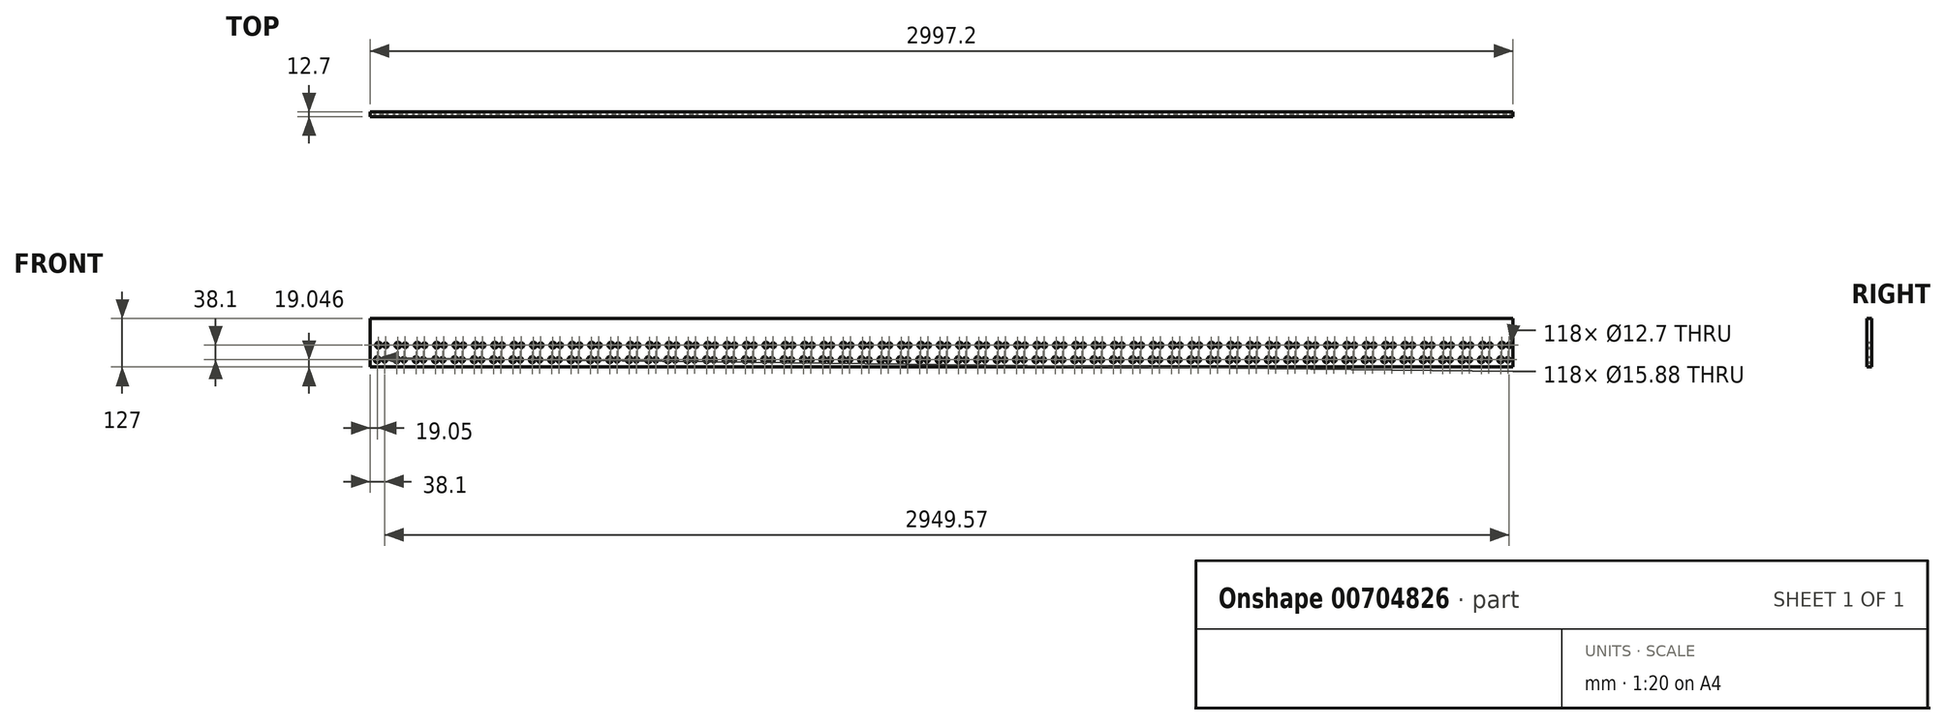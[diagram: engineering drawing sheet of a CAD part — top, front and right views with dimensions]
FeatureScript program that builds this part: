
annotation { "Feature Type Name" : "Feature", "Feature Type Description" : "" }
export const myFeature = defineFeature(function(context is Context, id is Id, definition is map)
    precondition{}
    {
        {
            var Q0;
            Q0=qCreatedBy(makeId("Front.planeOp"),FACE);
            var sketch = newSketch(context, id + "F0", { "sketchPlane" : qUnion([Q0])});
            skLineSegment(sketch, "E0.bottom", {"start": v(0, 309.84) * mm, "end": v(2997.2, 309.84) * mm});
            skLineSegment(sketch, "E0.top", {"start": v(0, 182.84) * mm, "end": v(2997.2, 182.84) * mm});
            skLineSegment(sketch, "E0.left", {"start": v(0, 309.84) * mm, "end": v(0, 182.84) * mm});
            skLineSegment(sketch, "E0.right", {"start": v(2997.2, 309.84) * mm, "end": v(2997.2, 182.84) * mm});
            skLineSegment(sketch, "E1.0", {"start": v(19.05, 201.89) * mm, "end": v(1200.15, 201.89) * mm});
            skCircle(sketch, "E2", {"center": v(19.05, 201.89) * mm, "radius": 7.94 * mm});
            skCircle(sketch, "E3", {"center": v(38.1, 201.89) * mm, "radius": 6.35 * mm});
            skLineSegment(sketch, "E4.direction1", {"start": v(19.05, 201.89) * mm, "end": v(69.85, 201.89) * mm, "construction": true});
            skLineSegment(sketch, "E5.0", {"start": v(19.05, 220.94) * mm, "end": v(1200.15, 220.94) * mm});
            skLineSegment(sketch, "E6.MirrorCS", {"start": v(19.05, 239.99) * mm, "end": v(1200.15, 239.99) * mm});
            skCircle(sketch, "E7.MirrorC", {"center": v(41.28, 239.99) * mm, "radius": 6.35 * mm});
            skCircle(sketch, "E8.MirrorC", {"center": v(22.23, 239.99) * mm, "radius": 7.94 * mm});
            skCircle(sketch, "E9.1.0.0", {"center": v(92.08, 239.99) * mm, "radius": 6.35 * mm});
            skCircle(sketch, "E9.1.0.1", {"center": v(73.03, 239.99) * mm, "radius": 7.94 * mm});
            skCircle(sketch, "E9.2.0.0", {"center": v(142.88, 239.99) * mm, "radius": 6.35 * mm});
            skCircle(sketch, "E9.2.0.1", {"center": v(123.83, 239.99) * mm, "radius": 7.94 * mm});
            skCircle(sketch, "E9.3.0.0", {"center": v(193.68, 239.99) * mm, "radius": 6.35 * mm});
            skCircle(sketch, "E9.3.0.1", {"center": v(174.63, 239.99) * mm, "radius": 7.94 * mm});
            skCircle(sketch, "E9.4.0.0", {"center": v(244.48, 239.99) * mm, "radius": 6.35 * mm});
            skCircle(sketch, "E9.4.0.1", {"center": v(225.43, 239.99) * mm, "radius": 7.94 * mm});
            skCircle(sketch, "E9.5.0.0", {"center": v(295.28, 239.99) * mm, "radius": 6.35 * mm});
            skCircle(sketch, "E9.5.0.1", {"center": v(276.23, 239.99) * mm, "radius": 7.94 * mm});
            skCircle(sketch, "E9.6.0.0", {"center": v(346.08, 239.99) * mm, "radius": 6.35 * mm});
            skCircle(sketch, "E9.6.0.1", {"center": v(327.03, 239.99) * mm, "radius": 7.94 * mm});
            skCircle(sketch, "E9.7.0.0", {"center": v(396.88, 239.99) * mm, "radius": 6.35 * mm});
            skCircle(sketch, "E9.7.0.1", {"center": v(377.83, 239.99) * mm, "radius": 7.94 * mm});
            skCircle(sketch, "E9.8.0.0", {"center": v(447.68, 239.99) * mm, "radius": 6.35 * mm});
            skCircle(sketch, "E9.8.0.1", {"center": v(428.63, 239.99) * mm, "radius": 7.94 * mm});
            skCircle(sketch, "E9.9.0.0", {"center": v(498.48, 239.99) * mm, "radius": 6.35 * mm});
            skCircle(sketch, "E9.9.0.1", {"center": v(479.43, 239.99) * mm, "radius": 7.94 * mm});
            skCircle(sketch, "E9.10.0.0", {"center": v(549.28, 239.99) * mm, "radius": 6.35 * mm});
            skCircle(sketch, "E9.10.0.1", {"center": v(530.23, 239.99) * mm, "radius": 7.94 * mm});
            skCircle(sketch, "E9.11.0.0", {"center": v(600.08, 239.99) * mm, "radius": 6.35 * mm});
            skCircle(sketch, "E9.11.0.1", {"center": v(581.03, 239.99) * mm, "radius": 7.94 * mm});
            skCircle(sketch, "E9.12.0.0", {"center": v(650.88, 239.99) * mm, "radius": 6.35 * mm});
            skCircle(sketch, "E9.12.0.1", {"center": v(631.83, 239.99) * mm, "radius": 7.94 * mm});
            skCircle(sketch, "E9.13.0.0", {"center": v(701.68, 239.99) * mm, "radius": 6.35 * mm});
            skCircle(sketch, "E9.13.0.1", {"center": v(682.63, 239.99) * mm, "radius": 7.94 * mm});
            skCircle(sketch, "E9.14.0.0", {"center": v(752.48, 239.99) * mm, "radius": 6.35 * mm});
            skCircle(sketch, "E9.14.0.1", {"center": v(733.43, 239.99) * mm, "radius": 7.94 * mm});
            skCircle(sketch, "E9.15.0.0", {"center": v(803.28, 239.99) * mm, "radius": 6.35 * mm});
            skCircle(sketch, "E9.15.0.1", {"center": v(784.23, 239.99) * mm, "radius": 7.94 * mm});
            skCircle(sketch, "E9.16.0.0", {"center": v(854.08, 239.99) * mm, "radius": 6.35 * mm});
            skCircle(sketch, "E9.16.0.1", {"center": v(835.03, 239.99) * mm, "radius": 7.94 * mm});
            skCircle(sketch, "E9.17.0.0", {"center": v(904.88, 239.99) * mm, "radius": 6.35 * mm});
            skCircle(sketch, "E9.17.0.1", {"center": v(885.83, 239.99) * mm, "radius": 7.94 * mm});
            skCircle(sketch, "E9.18.0.0", {"center": v(955.68, 239.99) * mm, "radius": 6.35 * mm});
            skCircle(sketch, "E9.18.0.1", {"center": v(936.63, 239.99) * mm, "radius": 7.94 * mm});
            skCircle(sketch, "E9.19.0.0", {"center": v(1006.48, 239.99) * mm, "radius": 6.35 * mm});
            skCircle(sketch, "E9.19.0.1", {"center": v(987.43, 239.99) * mm, "radius": 7.94 * mm});
            skCircle(sketch, "E9.20.0.0", {"center": v(1057.28, 239.99) * mm, "radius": 6.35 * mm});
            skCircle(sketch, "E9.20.0.1", {"center": v(1038.23, 239.99) * mm, "radius": 7.94 * mm});
            skCircle(sketch, "E9.21.0.0", {"center": v(1108.08, 239.99) * mm, "radius": 6.35 * mm});
            skCircle(sketch, "E9.21.0.1", {"center": v(1089.03, 239.99) * mm, "radius": 7.94 * mm});
            skCircle(sketch, "E9.22.0.0", {"center": v(1158.88, 239.99) * mm, "radius": 6.35 * mm});
            skCircle(sketch, "E9.22.0.1", {"center": v(1139.83, 239.99) * mm, "radius": 7.94 * mm});
            skCircle(sketch, "E9.23.0.0", {"center": v(1209.68, 239.99) * mm, "radius": 6.35 * mm});
            skCircle(sketch, "E9.23.0.1", {"center": v(1190.63, 239.99) * mm, "radius": 7.94 * mm});
            skCircle(sketch, "E9.24.0.0", {"center": v(1260.48, 239.99) * mm, "radius": 6.35 * mm});
            skCircle(sketch, "E9.24.0.1", {"center": v(1241.43, 239.99) * mm, "radius": 7.94 * mm});
            skLineSegment(sketch, "E9.direction1", {"start": v(41.28, 239.99) * mm, "end": v(92.08, 239.99) * mm, "construction": true});
            skCircle(sketch, "E10.1.0.0", {"center": v(69.85, 201.89) * mm, "radius": 7.94 * mm});
            skCircle(sketch, "E10.1.0.1", {"center": v(88.9, 201.89) * mm, "radius": 6.35 * mm});
            skCircle(sketch, "E10.2.0.0", {"center": v(120.65, 201.89) * mm, "radius": 7.94 * mm});
            skCircle(sketch, "E10.2.0.1", {"center": v(139.7, 201.89) * mm, "radius": 6.35 * mm});
            skCircle(sketch, "E10.3.0.0", {"center": v(171.45, 201.89) * mm, "radius": 7.94 * mm});
            skCircle(sketch, "E10.3.0.1", {"center": v(190.5, 201.89) * mm, "radius": 6.35 * mm});
            skCircle(sketch, "E10.4.0.0", {"center": v(222.25, 201.89) * mm, "radius": 7.94 * mm});
            skCircle(sketch, "E10.4.0.1", {"center": v(241.3, 201.89) * mm, "radius": 6.35 * mm});
            skCircle(sketch, "E10.5.0.0", {"center": v(273.05, 201.89) * mm, "radius": 7.94 * mm});
            skCircle(sketch, "E10.5.0.1", {"center": v(292.1, 201.89) * mm, "radius": 6.35 * mm});
            skCircle(sketch, "E10.6.0.0", {"center": v(323.85, 201.89) * mm, "radius": 7.94 * mm});
            skCircle(sketch, "E10.6.0.1", {"center": v(342.9, 201.89) * mm, "radius": 6.35 * mm});
            skCircle(sketch, "E10.7.0.0", {"center": v(374.65, 201.89) * mm, "radius": 7.94 * mm});
            skCircle(sketch, "E10.7.0.1", {"center": v(393.7, 201.89) * mm, "radius": 6.35 * mm});
            skCircle(sketch, "E10.8.0.0", {"center": v(425.45, 201.89) * mm, "radius": 7.94 * mm});
            skCircle(sketch, "E10.8.0.1", {"center": v(444.5, 201.89) * mm, "radius": 6.35 * mm});
            skCircle(sketch, "E10.9.0.0", {"center": v(476.25, 201.89) * mm, "radius": 7.94 * mm});
            skCircle(sketch, "E10.9.0.1", {"center": v(495.3, 201.89) * mm, "radius": 6.35 * mm});
            skCircle(sketch, "E10.10.0.0", {"center": v(527.05, 201.89) * mm, "radius": 7.94 * mm});
            skCircle(sketch, "E10.10.0.1", {"center": v(546.1, 201.89) * mm, "radius": 6.35 * mm});
            skCircle(sketch, "E10.11.0.0", {"center": v(577.85, 201.89) * mm, "radius": 7.94 * mm});
            skCircle(sketch, "E10.11.0.1", {"center": v(596.9, 201.89) * mm, "radius": 6.35 * mm});
            skCircle(sketch, "E10.12.0.0", {"center": v(628.65, 201.89) * mm, "radius": 7.94 * mm});
            skCircle(sketch, "E10.12.0.1", {"center": v(647.7, 201.89) * mm, "radius": 6.35 * mm});
            skCircle(sketch, "E10.13.0.0", {"center": v(679.45, 201.89) * mm, "radius": 7.94 * mm});
            skCircle(sketch, "E10.13.0.1", {"center": v(698.5, 201.89) * mm, "radius": 6.35 * mm});
            skCircle(sketch, "E10.14.0.0", {"center": v(730.25, 201.89) * mm, "radius": 7.94 * mm});
            skCircle(sketch, "E10.14.0.1", {"center": v(749.3, 201.89) * mm, "radius": 6.35 * mm});
            skCircle(sketch, "E10.15.0.0", {"center": v(781.05, 201.89) * mm, "radius": 7.94 * mm});
            skCircle(sketch, "E10.15.0.1", {"center": v(800.1, 201.89) * mm, "radius": 6.35 * mm});
            skCircle(sketch, "E10.16.0.0", {"center": v(831.85, 201.89) * mm, "radius": 7.94 * mm});
            skCircle(sketch, "E10.16.0.1", {"center": v(850.9, 201.89) * mm, "radius": 6.35 * mm});
            skCircle(sketch, "E10.17.0.0", {"center": v(882.65, 201.89) * mm, "radius": 7.94 * mm});
            skCircle(sketch, "E10.17.0.1", {"center": v(901.7, 201.89) * mm, "radius": 6.35 * mm});
            skCircle(sketch, "E10.18.0.0", {"center": v(933.45, 201.89) * mm, "radius": 7.94 * mm});
            skCircle(sketch, "E10.18.0.1", {"center": v(952.5, 201.89) * mm, "radius": 6.35 * mm});
            skCircle(sketch, "E10.19.0.0", {"center": v(984.25, 201.89) * mm, "radius": 7.94 * mm});
            skCircle(sketch, "E10.19.0.1", {"center": v(1003.3, 201.89) * mm, "radius": 6.35 * mm});
            skCircle(sketch, "E10.20.0.0", {"center": v(1035.05, 201.89) * mm, "radius": 7.94 * mm});
            skCircle(sketch, "E10.20.0.1", {"center": v(1054.1, 201.89) * mm, "radius": 6.35 * mm});
            skCircle(sketch, "E10.21.0.0", {"center": v(1085.85, 201.89) * mm, "radius": 7.94 * mm});
            skCircle(sketch, "E10.21.0.1", {"center": v(1104.9, 201.89) * mm, "radius": 6.35 * mm});
            skCircle(sketch, "E10.22.0.0", {"center": v(1136.65, 201.89) * mm, "radius": 7.94 * mm});
            skCircle(sketch, "E10.22.0.1", {"center": v(1155.7, 201.89) * mm, "radius": 6.35 * mm});
            skCircle(sketch, "E10.23.0.0", {"center": v(1187.45, 201.89) * mm, "radius": 7.94 * mm});
            skCircle(sketch, "E10.23.0.1", {"center": v(1206.5, 201.89) * mm, "radius": 6.35 * mm});
            skCircle(sketch, "E10.24.0.0", {"center": v(1238.25, 201.89) * mm, "radius": 7.94 * mm});
            skCircle(sketch, "E10.24.0.1", {"center": v(1257.3, 201.89) * mm, "radius": 6.35 * mm});
            skCircle(sketch, "E11.0.25.0", {"center": v(1311.28, 239.99) * mm, "radius": 6.35 * mm});
            skCircle(sketch, "E11.2.25.0", {"center": v(1292.23, 239.99) * mm, "radius": 7.94 * mm});
            skCircle(sketch, "E11.0.26.0", {"center": v(1362.08, 239.99) * mm, "radius": 6.35 * mm});
            skCircle(sketch, "E11.2.26.0", {"center": v(1343.03, 239.99) * mm, "radius": 7.94 * mm});
            skCircle(sketch, "E11.0.27.0", {"center": v(1412.88, 239.99) * mm, "radius": 6.35 * mm});
            skCircle(sketch, "E11.2.27.0", {"center": v(1393.83, 239.99) * mm, "radius": 7.94 * mm});
            skCircle(sketch, "E11.0.28.0", {"center": v(1463.68, 239.99) * mm, "radius": 6.35 * mm});
            skCircle(sketch, "E11.2.28.0", {"center": v(1444.63, 239.99) * mm, "radius": 7.94 * mm});
            skCircle(sketch, "E11.0.29.0", {"center": v(1514.48, 239.99) * mm, "radius": 6.35 * mm});
            skCircle(sketch, "E11.2.29.0", {"center": v(1495.43, 239.99) * mm, "radius": 7.94 * mm});
            skCircle(sketch, "E11.0.30.0", {"center": v(1565.28, 239.99) * mm, "radius": 6.35 * mm});
            skCircle(sketch, "E11.2.30.0", {"center": v(1546.23, 239.99) * mm, "radius": 7.94 * mm});
            skCircle(sketch, "E11.0.31.0", {"center": v(1616.08, 239.99) * mm, "radius": 6.35 * mm});
            skCircle(sketch, "E11.2.31.0", {"center": v(1597.03, 239.99) * mm, "radius": 7.94 * mm});
            skCircle(sketch, "E11.0.32.0", {"center": v(1666.88, 239.99) * mm, "radius": 6.35 * mm});
            skCircle(sketch, "E11.2.32.0", {"center": v(1647.83, 239.99) * mm, "radius": 7.94 * mm});
            skCircle(sketch, "E11.0.33.0", {"center": v(1717.68, 239.99) * mm, "radius": 6.35 * mm});
            skCircle(sketch, "E11.2.33.0", {"center": v(1698.63, 239.99) * mm, "radius": 7.94 * mm});
            skCircle(sketch, "E11.0.34.0", {"center": v(1768.48, 239.99) * mm, "radius": 6.35 * mm});
            skCircle(sketch, "E11.2.34.0", {"center": v(1749.43, 239.99) * mm, "radius": 7.94 * mm});
            skCircle(sketch, "E11.0.35.0", {"center": v(1819.28, 239.99) * mm, "radius": 6.35 * mm});
            skCircle(sketch, "E11.2.35.0", {"center": v(1800.23, 239.99) * mm, "radius": 7.94 * mm});
            skCircle(sketch, "E11.0.36.0", {"center": v(1870.08, 239.99) * mm, "radius": 6.35 * mm});
            skCircle(sketch, "E11.2.36.0", {"center": v(1851.03, 239.99) * mm, "radius": 7.94 * mm});
            skCircle(sketch, "E11.0.37.0", {"center": v(1920.88, 239.99) * mm, "radius": 6.35 * mm});
            skCircle(sketch, "E11.2.37.0", {"center": v(1901.83, 239.99) * mm, "radius": 7.94 * mm});
            skCircle(sketch, "E11.0.38.0", {"center": v(1971.68, 239.99) * mm, "radius": 6.35 * mm});
            skCircle(sketch, "E11.2.38.0", {"center": v(1952.63, 239.99) * mm, "radius": 7.94 * mm});
            skCircle(sketch, "E11.0.39.0", {"center": v(2022.48, 239.99) * mm, "radius": 6.35 * mm});
            skCircle(sketch, "E11.2.39.0", {"center": v(2003.43, 239.99) * mm, "radius": 7.94 * mm});
            skCircle(sketch, "E11.0.40.0", {"center": v(2073.28, 239.99) * mm, "radius": 6.35 * mm});
            skCircle(sketch, "E11.2.40.0", {"center": v(2054.23, 239.99) * mm, "radius": 7.94 * mm});
            skCircle(sketch, "E11.0.41.0", {"center": v(2124.08, 239.99) * mm, "radius": 6.35 * mm});
            skCircle(sketch, "E11.2.41.0", {"center": v(2105.03, 239.99) * mm, "radius": 7.94 * mm});
            skCircle(sketch, "E11.0.42.0", {"center": v(2174.88, 239.99) * mm, "radius": 6.35 * mm});
            skCircle(sketch, "E11.2.42.0", {"center": v(2155.83, 239.99) * mm, "radius": 7.94 * mm});
            skCircle(sketch, "E11.0.43.0", {"center": v(2225.68, 239.99) * mm, "radius": 6.35 * mm});
            skCircle(sketch, "E11.2.43.0", {"center": v(2206.63, 239.99) * mm, "radius": 7.94 * mm});
            skCircle(sketch, "E11.0.44.0", {"center": v(2276.48, 239.99) * mm, "radius": 6.35 * mm});
            skCircle(sketch, "E11.2.44.0", {"center": v(2257.43, 239.99) * mm, "radius": 7.94 * mm});
            skCircle(sketch, "E11.0.45.0", {"center": v(2327.28, 239.99) * mm, "radius": 6.35 * mm});
            skCircle(sketch, "E11.2.45.0", {"center": v(2308.23, 239.99) * mm, "radius": 7.94 * mm});
            skCircle(sketch, "E11.0.46.0", {"center": v(2378.08, 239.99) * mm, "radius": 6.35 * mm});
            skCircle(sketch, "E11.2.46.0", {"center": v(2359.03, 239.99) * mm, "radius": 7.94 * mm});
            skCircle(sketch, "E11.0.47.0", {"center": v(2428.88, 239.99) * mm, "radius": 6.35 * mm});
            skCircle(sketch, "E11.2.47.0", {"center": v(2409.83, 239.99) * mm, "radius": 7.94 * mm});
            skCircle(sketch, "E11.0.48.0", {"center": v(2479.68, 239.99) * mm, "radius": 6.35 * mm});
            skCircle(sketch, "E11.2.48.0", {"center": v(2460.63, 239.99) * mm, "radius": 7.94 * mm});
            skCircle(sketch, "E11.0.49.0", {"center": v(2530.48, 239.99) * mm, "radius": 6.35 * mm});
            skCircle(sketch, "E11.2.49.0", {"center": v(2511.43, 239.99) * mm, "radius": 7.94 * mm});
            skCircle(sketch, "E12.0.25.0", {"center": v(1289.05, 201.89) * mm, "radius": 7.94 * mm});
            skCircle(sketch, "E12.2.25.0", {"center": v(1308.1, 201.89) * mm, "radius": 6.35 * mm});
            skCircle(sketch, "E12.0.26.0", {"center": v(1339.85, 201.89) * mm, "radius": 7.94 * mm});
            skCircle(sketch, "E12.2.26.0", {"center": v(1358.9, 201.89) * mm, "radius": 6.35 * mm});
            skCircle(sketch, "E12.0.27.0", {"center": v(1390.65, 201.89) * mm, "radius": 7.94 * mm});
            skCircle(sketch, "E12.2.27.0", {"center": v(1409.7, 201.89) * mm, "radius": 6.35 * mm});
            skCircle(sketch, "E12.0.28.0", {"center": v(1441.45, 201.89) * mm, "radius": 7.94 * mm});
            skCircle(sketch, "E12.2.28.0", {"center": v(1460.5, 201.89) * mm, "radius": 6.35 * mm});
            skCircle(sketch, "E12.0.29.0", {"center": v(1492.25, 201.89) * mm, "radius": 7.94 * mm});
            skCircle(sketch, "E12.2.29.0", {"center": v(1511.3, 201.89) * mm, "radius": 6.35 * mm});
            skCircle(sketch, "E12.0.30.0", {"center": v(1543.05, 201.89) * mm, "radius": 7.94 * mm});
            skCircle(sketch, "E12.2.30.0", {"center": v(1562.1, 201.89) * mm, "radius": 6.35 * mm});
            skCircle(sketch, "E12.0.31.0", {"center": v(1593.85, 201.89) * mm, "radius": 7.94 * mm});
            skCircle(sketch, "E12.2.31.0", {"center": v(1612.9, 201.89) * mm, "radius": 6.35 * mm});
            skCircle(sketch, "E12.0.32.0", {"center": v(1644.65, 201.89) * mm, "radius": 7.94 * mm});
            skCircle(sketch, "E12.2.32.0", {"center": v(1663.7, 201.89) * mm, "radius": 6.35 * mm});
            skCircle(sketch, "E12.0.33.0", {"center": v(1695.45, 201.89) * mm, "radius": 7.94 * mm});
            skCircle(sketch, "E12.2.33.0", {"center": v(1714.5, 201.89) * mm, "radius": 6.35 * mm});
            skCircle(sketch, "E12.0.34.0", {"center": v(1746.25, 201.89) * mm, "radius": 7.94 * mm});
            skCircle(sketch, "E12.2.34.0", {"center": v(1765.3, 201.89) * mm, "radius": 6.35 * mm});
            skCircle(sketch, "E12.0.35.0", {"center": v(1797.05, 201.89) * mm, "radius": 7.94 * mm});
            skCircle(sketch, "E12.2.35.0", {"center": v(1816.1, 201.89) * mm, "radius": 6.35 * mm});
            skCircle(sketch, "E12.0.36.0", {"center": v(1847.85, 201.89) * mm, "radius": 7.94 * mm});
            skCircle(sketch, "E12.2.36.0", {"center": v(1866.9, 201.89) * mm, "radius": 6.35 * mm});
            skCircle(sketch, "E12.0.37.0", {"center": v(1898.65, 201.89) * mm, "radius": 7.94 * mm});
            skCircle(sketch, "E12.2.37.0", {"center": v(1917.7, 201.89) * mm, "radius": 6.35 * mm});
            skCircle(sketch, "E12.0.38.0", {"center": v(1949.45, 201.89) * mm, "radius": 7.94 * mm});
            skCircle(sketch, "E12.2.38.0", {"center": v(1968.5, 201.89) * mm, "radius": 6.35 * mm});
            skCircle(sketch, "E12.0.39.0", {"center": v(2000.25, 201.89) * mm, "radius": 7.94 * mm});
            skCircle(sketch, "E12.2.39.0", {"center": v(2019.3, 201.89) * mm, "radius": 6.35 * mm});
            skCircle(sketch, "E12.0.40.0", {"center": v(2051.05, 201.89) * mm, "radius": 7.94 * mm});
            skCircle(sketch, "E12.2.40.0", {"center": v(2070.1, 201.89) * mm, "radius": 6.35 * mm});
            skCircle(sketch, "E12.0.41.0", {"center": v(2101.85, 201.89) * mm, "radius": 7.94 * mm});
            skCircle(sketch, "E12.2.41.0", {"center": v(2120.9, 201.89) * mm, "radius": 6.35 * mm});
            skCircle(sketch, "E12.0.42.0", {"center": v(2152.65, 201.89) * mm, "radius": 7.94 * mm});
            skCircle(sketch, "E12.2.42.0", {"center": v(2171.7, 201.89) * mm, "radius": 6.35 * mm});
            skCircle(sketch, "E12.0.43.0", {"center": v(2203.45, 201.89) * mm, "radius": 7.94 * mm});
            skCircle(sketch, "E12.2.43.0", {"center": v(2222.5, 201.89) * mm, "radius": 6.35 * mm});
            skCircle(sketch, "E12.0.44.0", {"center": v(2254.25, 201.89) * mm, "radius": 7.94 * mm});
            skCircle(sketch, "E12.2.44.0", {"center": v(2273.3, 201.89) * mm, "radius": 6.35 * mm});
            skCircle(sketch, "E12.0.45.0", {"center": v(2305.05, 201.89) * mm, "radius": 7.94 * mm});
            skCircle(sketch, "E12.2.45.0", {"center": v(2324.1, 201.89) * mm, "radius": 6.35 * mm});
            skCircle(sketch, "E12.0.46.0", {"center": v(2355.85, 201.89) * mm, "radius": 7.94 * mm});
            skCircle(sketch, "E12.2.46.0", {"center": v(2374.9, 201.89) * mm, "radius": 6.35 * mm});
            skCircle(sketch, "E12.0.47.0", {"center": v(2406.65, 201.89) * mm, "radius": 7.94 * mm});
            skCircle(sketch, "E12.2.47.0", {"center": v(2425.7, 201.89) * mm, "radius": 6.35 * mm});
            skCircle(sketch, "E12.0.48.0", {"center": v(2457.45, 201.89) * mm, "radius": 7.94 * mm});
            skCircle(sketch, "E12.2.48.0", {"center": v(2476.5, 201.89) * mm, "radius": 6.35 * mm});
            skCircle(sketch, "E12.0.49.0", {"center": v(2508.25, 201.89) * mm, "radius": 7.94 * mm});
            skCircle(sketch, "E12.2.49.0", {"center": v(2527.3, 201.89) * mm, "radius": 6.35 * mm});
            skCircle(sketch, "E13.0.50.0", {"center": v(2581.28, 239.99) * mm, "radius": 6.35 * mm});
            skCircle(sketch, "E13.2.50.0", {"center": v(2562.23, 239.99) * mm, "radius": 7.94 * mm});
            skCircle(sketch, "E13.0.51.0", {"center": v(2632.08, 239.99) * mm, "radius": 6.35 * mm});
            skCircle(sketch, "E13.2.51.0", {"center": v(2613.03, 239.99) * mm, "radius": 7.94 * mm});
            skCircle(sketch, "E13.0.52.0", {"center": v(2682.88, 239.99) * mm, "radius": 6.35 * mm});
            skCircle(sketch, "E13.2.52.0", {"center": v(2663.83, 239.99) * mm, "radius": 7.94 * mm});
            skCircle(sketch, "E13.0.53.0", {"center": v(2733.68, 239.99) * mm, "radius": 6.35 * mm});
            skCircle(sketch, "E13.2.53.0", {"center": v(2714.63, 239.99) * mm, "radius": 7.94 * mm});
            skCircle(sketch, "E13.0.54.0", {"center": v(2784.48, 239.99) * mm, "radius": 6.35 * mm});
            skCircle(sketch, "E13.2.54.0", {"center": v(2765.43, 239.99) * mm, "radius": 7.94 * mm});
            skCircle(sketch, "E13.0.55.0", {"center": v(2835.28, 239.99) * mm, "radius": 6.35 * mm});
            skCircle(sketch, "E13.2.55.0", {"center": v(2816.23, 239.99) * mm, "radius": 7.94 * mm});
            skCircle(sketch, "E13.0.56.0", {"center": v(2886.08, 239.99) * mm, "radius": 6.35 * mm});
            skCircle(sketch, "E13.2.56.0", {"center": v(2867.03, 239.99) * mm, "radius": 7.94 * mm});
            skCircle(sketch, "E13.0.57.0", {"center": v(2936.88, 239.99) * mm, "radius": 6.35 * mm});
            skCircle(sketch, "E13.2.57.0", {"center": v(2917.83, 239.99) * mm, "radius": 7.94 * mm});
            skCircle(sketch, "E13.0.58.0", {"center": v(2987.68, 239.99) * mm, "radius": 6.35 * mm});
            skCircle(sketch, "E13.2.58.0", {"center": v(2968.63, 239.99) * mm, "radius": 7.94 * mm});
            skCircle(sketch, "E13.0.59.0", {"center": v(3038.48, 239.99) * mm, "radius": 6.35 * mm});
            skCircle(sketch, "E13.2.59.0", {"center": v(3019.43, 239.99) * mm, "radius": 7.94 * mm});
            skCircle(sketch, "E13.0.60.0", {"center": v(3089.28, 239.99) * mm, "radius": 6.35 * mm});
            skCircle(sketch, "E13.2.60.0", {"center": v(3070.23, 239.99) * mm, "radius": 7.94 * mm});
            skCircle(sketch, "E13.0.61.0", {"center": v(3140.08, 239.99) * mm, "radius": 6.35 * mm});
            skCircle(sketch, "E13.2.61.0", {"center": v(3121.03, 239.99) * mm, "radius": 7.94 * mm});
            skCircle(sketch, "E13.0.62.0", {"center": v(3190.88, 239.99) * mm, "radius": 6.35 * mm});
            skCircle(sketch, "E13.2.62.0", {"center": v(3171.83, 239.99) * mm, "radius": 7.94 * mm});
            skCircle(sketch, "E13.0.63.0", {"center": v(3241.68, 239.99) * mm, "radius": 6.35 * mm});
            skCircle(sketch, "E13.2.63.0", {"center": v(3222.63, 239.99) * mm, "radius": 7.94 * mm});
            skCircle(sketch, "E13.0.64.0", {"center": v(3292.48, 239.99) * mm, "radius": 6.35 * mm});
            skCircle(sketch, "E13.2.64.0", {"center": v(3273.43, 239.99) * mm, "radius": 7.94 * mm});
            skCircle(sketch, "E13.0.65.0", {"center": v(3343.28, 239.99) * mm, "radius": 6.35 * mm});
            skCircle(sketch, "E13.2.65.0", {"center": v(3324.23, 239.99) * mm, "radius": 7.94 * mm});
            skCircle(sketch, "E13.0.66.0", {"center": v(3394.08, 239.99) * mm, "radius": 6.35 * mm});
            skCircle(sketch, "E13.2.66.0", {"center": v(3375.03, 239.99) * mm, "radius": 7.94 * mm});
            skCircle(sketch, "E13.0.67.0", {"center": v(3444.88, 239.99) * mm, "radius": 6.35 * mm});
            skCircle(sketch, "E13.2.67.0", {"center": v(3425.83, 239.99) * mm, "radius": 7.94 * mm});
            skCircle(sketch, "E13.0.68.0", {"center": v(3495.68, 239.99) * mm, "radius": 6.35 * mm});
            skCircle(sketch, "E13.2.68.0", {"center": v(3476.63, 239.99) * mm, "radius": 7.94 * mm});
            skCircle(sketch, "E13.0.69.0", {"center": v(3546.48, 239.99) * mm, "radius": 6.35 * mm});
            skCircle(sketch, "E13.2.69.0", {"center": v(3527.43, 239.99) * mm, "radius": 7.94 * mm});
            skCircle(sketch, "E13.0.70.0", {"center": v(3597.28, 239.99) * mm, "radius": 6.35 * mm});
            skCircle(sketch, "E13.2.70.0", {"center": v(3578.23, 239.99) * mm, "radius": 7.94 * mm});
            skCircle(sketch, "E13.0.71.0", {"center": v(3648.08, 239.99) * mm, "radius": 6.35 * mm});
            skCircle(sketch, "E13.2.71.0", {"center": v(3629.03, 239.99) * mm, "radius": 7.94 * mm});
            skCircle(sketch, "E13.0.72.0", {"center": v(3698.88, 239.99) * mm, "radius": 6.35 * mm});
            skCircle(sketch, "E13.2.72.0", {"center": v(3679.83, 239.99) * mm, "radius": 7.94 * mm});
            skCircle(sketch, "E13.0.73.0", {"center": v(3749.68, 239.99) * mm, "radius": 6.35 * mm});
            skCircle(sketch, "E13.2.73.0", {"center": v(3730.63, 239.99) * mm, "radius": 7.94 * mm});
            skCircle(sketch, "E13.0.74.0", {"center": v(3800.48, 239.99) * mm, "radius": 6.35 * mm});
            skCircle(sketch, "E13.2.74.0", {"center": v(3781.43, 239.99) * mm, "radius": 7.94 * mm});
            skCircle(sketch, "E13.0.75.0", {"center": v(3851.28, 239.99) * mm, "radius": 6.35 * mm});
            skCircle(sketch, "E13.2.75.0", {"center": v(3832.23, 239.99) * mm, "radius": 7.94 * mm});
            skCircle(sketch, "E13.0.76.0", {"center": v(3902.08, 239.99) * mm, "radius": 6.35 * mm});
            skCircle(sketch, "E13.2.76.0", {"center": v(3883.03, 239.99) * mm, "radius": 7.94 * mm});
            skCircle(sketch, "E13.0.77.0", {"center": v(3952.88, 239.99) * mm, "radius": 6.35 * mm});
            skCircle(sketch, "E13.2.77.0", {"center": v(3933.83, 239.99) * mm, "radius": 7.94 * mm});
            skCircle(sketch, "E13.0.78.0", {"center": v(4003.68, 239.99) * mm, "radius": 6.35 * mm});
            skCircle(sketch, "E13.2.78.0", {"center": v(3984.63, 239.99) * mm, "radius": 7.94 * mm});
            skCircle(sketch, "E13.0.79.0", {"center": v(4054.48, 239.99) * mm, "radius": 6.35 * mm});
            skCircle(sketch, "E13.2.79.0", {"center": v(4035.43, 239.99) * mm, "radius": 7.94 * mm});
            skCircle(sketch, "E13.0.80.0", {"center": v(4105.28, 239.99) * mm, "radius": 6.35 * mm});
            skCircle(sketch, "E13.2.80.0", {"center": v(4086.23, 239.99) * mm, "radius": 7.94 * mm});
            skCircle(sketch, "E13.0.81.0", {"center": v(4156.08, 239.99) * mm, "radius": 6.35 * mm});
            skCircle(sketch, "E13.2.81.0", {"center": v(4137.03, 239.99) * mm, "radius": 7.94 * mm});
            skCircle(sketch, "E13.0.82.0", {"center": v(4206.88, 239.99) * mm, "radius": 6.35 * mm});
            skCircle(sketch, "E13.2.82.0", {"center": v(4187.83, 239.99) * mm, "radius": 7.94 * mm});
            skCircle(sketch, "E13.0.83.0", {"center": v(4257.68, 239.99) * mm, "radius": 6.35 * mm});
            skCircle(sketch, "E13.2.83.0", {"center": v(4238.63, 239.99) * mm, "radius": 7.94 * mm});
            skCircle(sketch, "E13.0.84.0", {"center": v(4308.48, 239.99) * mm, "radius": 6.35 * mm});
            skCircle(sketch, "E13.2.84.0", {"center": v(4289.43, 239.99) * mm, "radius": 7.94 * mm});
            skCircle(sketch, "E13.0.85.0", {"center": v(4359.28, 239.99) * mm, "radius": 6.35 * mm});
            skCircle(sketch, "E13.2.85.0", {"center": v(4340.23, 239.99) * mm, "radius": 7.94 * mm});
            skCircle(sketch, "E13.0.86.0", {"center": v(4410.08, 239.99) * mm, "radius": 6.35 * mm});
            skCircle(sketch, "E13.2.86.0", {"center": v(4391.03, 239.99) * mm, "radius": 7.94 * mm});
            skCircle(sketch, "E13.0.87.0", {"center": v(4460.88, 239.99) * mm, "radius": 6.35 * mm});
            skCircle(sketch, "E13.2.87.0", {"center": v(4441.83, 239.99) * mm, "radius": 7.94 * mm});
            skCircle(sketch, "E13.0.88.0", {"center": v(4511.68, 239.99) * mm, "radius": 6.35 * mm});
            skCircle(sketch, "E13.2.88.0", {"center": v(4492.63, 239.99) * mm, "radius": 7.94 * mm});
            skCircle(sketch, "E13.0.89.0", {"center": v(4562.48, 239.99) * mm, "radius": 6.35 * mm});
            skCircle(sketch, "E13.2.89.0", {"center": v(4543.43, 239.99) * mm, "radius": 7.94 * mm});
            skCircle(sketch, "E13.0.90.0", {"center": v(4613.28, 239.99) * mm, "radius": 6.35 * mm});
            skCircle(sketch, "E13.2.90.0", {"center": v(4594.23, 239.99) * mm, "radius": 7.94 * mm});
            skCircle(sketch, "E13.0.91.0", {"center": v(4664.08, 239.99) * mm, "radius": 6.35 * mm});
            skCircle(sketch, "E13.2.91.0", {"center": v(4645.03, 239.99) * mm, "radius": 7.94 * mm});
            skCircle(sketch, "E13.0.92.0", {"center": v(4714.88, 239.99) * mm, "radius": 6.35 * mm});
            skCircle(sketch, "E13.2.92.0", {"center": v(4695.83, 239.99) * mm, "radius": 7.94 * mm});
            skCircle(sketch, "E13.0.93.0", {"center": v(4765.68, 239.99) * mm, "radius": 6.35 * mm});
            skCircle(sketch, "E13.2.93.0", {"center": v(4746.63, 239.99) * mm, "radius": 7.94 * mm});
            skCircle(sketch, "E13.0.94.0", {"center": v(4816.48, 239.99) * mm, "radius": 6.35 * mm});
            skCircle(sketch, "E13.2.94.0", {"center": v(4797.43, 239.99) * mm, "radius": 7.94 * mm});
            skCircle(sketch, "E13.0.95.0", {"center": v(4867.28, 239.99) * mm, "radius": 6.35 * mm});
            skCircle(sketch, "E13.2.95.0", {"center": v(4848.23, 239.99) * mm, "radius": 7.94 * mm});
            skCircle(sketch, "E13.0.96.0", {"center": v(4918.08, 239.99) * mm, "radius": 6.35 * mm});
            skCircle(sketch, "E13.2.96.0", {"center": v(4899.03, 239.99) * mm, "radius": 7.94 * mm});
            skCircle(sketch, "E13.0.97.0", {"center": v(4968.88, 239.99) * mm, "radius": 6.35 * mm});
            skCircle(sketch, "E13.2.97.0", {"center": v(4949.83, 239.99) * mm, "radius": 7.94 * mm});
            skCircle(sketch, "E13.0.98.0", {"center": v(5019.68, 239.99) * mm, "radius": 6.35 * mm});
            skCircle(sketch, "E13.2.98.0", {"center": v(5000.63, 239.99) * mm, "radius": 7.94 * mm});
            skCircle(sketch, "E13.0.99.0", {"center": v(5070.48, 239.99) * mm, "radius": 6.35 * mm});
            skCircle(sketch, "E13.2.99.0", {"center": v(5051.43, 239.99) * mm, "radius": 7.94 * mm});
            skCircle(sketch, "E14.0.50.0", {"center": v(2559.05, 201.89) * mm, "radius": 7.94 * mm});
            skCircle(sketch, "E14.2.50.0", {"center": v(2578.1, 201.89) * mm, "radius": 6.35 * mm});
            skCircle(sketch, "E14.0.51.0", {"center": v(2609.85, 201.89) * mm, "radius": 7.94 * mm});
            skCircle(sketch, "E14.2.51.0", {"center": v(2628.9, 201.89) * mm, "radius": 6.35 * mm});
            skCircle(sketch, "E14.0.52.0", {"center": v(2660.65, 201.89) * mm, "radius": 7.94 * mm});
            skCircle(sketch, "E14.2.52.0", {"center": v(2679.7, 201.89) * mm, "radius": 6.35 * mm});
            skCircle(sketch, "E14.0.53.0", {"center": v(2711.45, 201.89) * mm, "radius": 7.94 * mm});
            skCircle(sketch, "E14.2.53.0", {"center": v(2730.5, 201.89) * mm, "radius": 6.35 * mm});
            skCircle(sketch, "E14.0.54.0", {"center": v(2762.25, 201.89) * mm, "radius": 7.94 * mm});
            skCircle(sketch, "E14.2.54.0", {"center": v(2781.3, 201.89) * mm, "radius": 6.35 * mm});
            skCircle(sketch, "E14.0.55.0", {"center": v(2813.05, 201.89) * mm, "radius": 7.94 * mm});
            skCircle(sketch, "E14.2.55.0", {"center": v(2832.1, 201.89) * mm, "radius": 6.35 * mm});
            skCircle(sketch, "E14.0.56.0", {"center": v(2863.85, 201.89) * mm, "radius": 7.94 * mm});
            skCircle(sketch, "E14.2.56.0", {"center": v(2882.9, 201.89) * mm, "radius": 6.35 * mm});
            skCircle(sketch, "E14.0.57.0", {"center": v(2914.65, 201.89) * mm, "radius": 7.94 * mm});
            skCircle(sketch, "E14.2.57.0", {"center": v(2933.7, 201.89) * mm, "radius": 6.35 * mm});
            skCircle(sketch, "E14.0.58.0", {"center": v(2965.45, 201.89) * mm, "radius": 7.94 * mm});
            skCircle(sketch, "E14.2.58.0", {"center": v(2984.5, 201.89) * mm, "radius": 6.35 * mm});
            skCircle(sketch, "E14.0.59.0", {"center": v(3016.25, 201.89) * mm, "radius": 7.94 * mm});
            skCircle(sketch, "E14.2.59.0", {"center": v(3035.3, 201.89) * mm, "radius": 6.35 * mm});
            skCircle(sketch, "E14.0.60.0", {"center": v(3067.05, 201.89) * mm, "radius": 7.94 * mm});
            skCircle(sketch, "E14.2.60.0", {"center": v(3086.1, 201.89) * mm, "radius": 6.35 * mm});
            skCircle(sketch, "E14.0.61.0", {"center": v(3117.85, 201.89) * mm, "radius": 7.94 * mm});
            skCircle(sketch, "E14.2.61.0", {"center": v(3136.9, 201.89) * mm, "radius": 6.35 * mm});
            skCircle(sketch, "E14.0.62.0", {"center": v(3168.65, 201.89) * mm, "radius": 7.94 * mm});
            skCircle(sketch, "E14.2.62.0", {"center": v(3187.7, 201.89) * mm, "radius": 6.35 * mm});
            skCircle(sketch, "E14.0.63.0", {"center": v(3219.45, 201.89) * mm, "radius": 7.94 * mm});
            skCircle(sketch, "E14.2.63.0", {"center": v(3238.5, 201.89) * mm, "radius": 6.35 * mm});
            skCircle(sketch, "E14.0.64.0", {"center": v(3270.25, 201.89) * mm, "radius": 7.94 * mm});
            skCircle(sketch, "E14.2.64.0", {"center": v(3289.3, 201.89) * mm, "radius": 6.35 * mm});
            skCircle(sketch, "E14.0.65.0", {"center": v(3321.05, 201.89) * mm, "radius": 7.94 * mm});
            skCircle(sketch, "E14.2.65.0", {"center": v(3340.1, 201.89) * mm, "radius": 6.35 * mm});
            skCircle(sketch, "E14.0.66.0", {"center": v(3371.85, 201.89) * mm, "radius": 7.94 * mm});
            skCircle(sketch, "E14.2.66.0", {"center": v(3390.9, 201.89) * mm, "radius": 6.35 * mm});
            skCircle(sketch, "E14.0.67.0", {"center": v(3422.65, 201.89) * mm, "radius": 7.94 * mm});
            skCircle(sketch, "E14.2.67.0", {"center": v(3441.7, 201.89) * mm, "radius": 6.35 * mm});
            skCircle(sketch, "E14.0.68.0", {"center": v(3473.45, 201.89) * mm, "radius": 7.94 * mm});
            skCircle(sketch, "E14.2.68.0", {"center": v(3492.5, 201.89) * mm, "radius": 6.35 * mm});
            skCircle(sketch, "E14.0.69.0", {"center": v(3524.25, 201.89) * mm, "radius": 7.94 * mm});
            skCircle(sketch, "E14.2.69.0", {"center": v(3543.3, 201.89) * mm, "radius": 6.35 * mm});
            skCircle(sketch, "E14.0.70.0", {"center": v(3575.05, 201.89) * mm, "radius": 7.94 * mm});
            skCircle(sketch, "E14.2.70.0", {"center": v(3594.1, 201.89) * mm, "radius": 6.35 * mm});
            skCircle(sketch, "E14.0.71.0", {"center": v(3625.85, 201.89) * mm, "radius": 7.94 * mm});
            skCircle(sketch, "E14.2.71.0", {"center": v(3644.9, 201.89) * mm, "radius": 6.35 * mm});
            skCircle(sketch, "E14.0.72.0", {"center": v(3676.65, 201.89) * mm, "radius": 7.94 * mm});
            skCircle(sketch, "E14.2.72.0", {"center": v(3695.7, 201.89) * mm, "radius": 6.35 * mm});
            skCircle(sketch, "E14.0.73.0", {"center": v(3727.45, 201.89) * mm, "radius": 7.94 * mm});
            skCircle(sketch, "E14.2.73.0", {"center": v(3746.5, 201.89) * mm, "radius": 6.35 * mm});
            skCircle(sketch, "E14.0.74.0", {"center": v(3778.25, 201.89) * mm, "radius": 7.94 * mm});
            skCircle(sketch, "E14.2.74.0", {"center": v(3797.3, 201.89) * mm, "radius": 6.35 * mm});
            skCircle(sketch, "E14.0.75.0", {"center": v(3829.05, 201.89) * mm, "radius": 7.94 * mm});
            skCircle(sketch, "E14.2.75.0", {"center": v(3848.1, 201.89) * mm, "radius": 6.35 * mm});
            skCircle(sketch, "E14.0.76.0", {"center": v(3879.85, 201.89) * mm, "radius": 7.94 * mm});
            skCircle(sketch, "E14.2.76.0", {"center": v(3898.9, 201.89) * mm, "radius": 6.35 * mm});
            skCircle(sketch, "E14.0.77.0", {"center": v(3930.65, 201.89) * mm, "radius": 7.94 * mm});
            skCircle(sketch, "E14.2.77.0", {"center": v(3949.7, 201.89) * mm, "radius": 6.35 * mm});
            skCircle(sketch, "E14.0.78.0", {"center": v(3981.45, 201.89) * mm, "radius": 7.94 * mm});
            skCircle(sketch, "E14.2.78.0", {"center": v(4000.5, 201.89) * mm, "radius": 6.35 * mm});
            skCircle(sketch, "E14.0.79.0", {"center": v(4032.25, 201.89) * mm, "radius": 7.94 * mm});
            skCircle(sketch, "E14.2.79.0", {"center": v(4051.3, 201.89) * mm, "radius": 6.35 * mm});
            skCircle(sketch, "E14.0.80.0", {"center": v(4083.05, 201.89) * mm, "radius": 7.94 * mm});
            skCircle(sketch, "E14.2.80.0", {"center": v(4102.1, 201.89) * mm, "radius": 6.35 * mm});
            skCircle(sketch, "E14.0.81.0", {"center": v(4133.85, 201.89) * mm, "radius": 7.94 * mm});
            skCircle(sketch, "E14.2.81.0", {"center": v(4152.9, 201.89) * mm, "radius": 6.35 * mm});
            skCircle(sketch, "E14.0.82.0", {"center": v(4184.65, 201.89) * mm, "radius": 7.94 * mm});
            skCircle(sketch, "E14.2.82.0", {"center": v(4203.7, 201.89) * mm, "radius": 6.35 * mm});
            skCircle(sketch, "E14.0.83.0", {"center": v(4235.45, 201.89) * mm, "radius": 7.94 * mm});
            skCircle(sketch, "E14.2.83.0", {"center": v(4254.5, 201.89) * mm, "radius": 6.35 * mm});
            skCircle(sketch, "E14.0.84.0", {"center": v(4286.25, 201.89) * mm, "radius": 7.94 * mm});
            skCircle(sketch, "E14.2.84.0", {"center": v(4305.3, 201.89) * mm, "radius": 6.35 * mm});
            skCircle(sketch, "E14.0.85.0", {"center": v(4337.05, 201.89) * mm, "radius": 7.94 * mm});
            skCircle(sketch, "E14.2.85.0", {"center": v(4356.1, 201.89) * mm, "radius": 6.35 * mm});
            skCircle(sketch, "E14.0.86.0", {"center": v(4387.85, 201.89) * mm, "radius": 7.94 * mm});
            skCircle(sketch, "E14.2.86.0", {"center": v(4406.9, 201.89) * mm, "radius": 6.35 * mm});
            skCircle(sketch, "E14.0.87.0", {"center": v(4438.65, 201.89) * mm, "radius": 7.94 * mm});
            skCircle(sketch, "E14.2.87.0", {"center": v(4457.7, 201.89) * mm, "radius": 6.35 * mm});
            skCircle(sketch, "E14.0.88.0", {"center": v(4489.45, 201.89) * mm, "radius": 7.94 * mm});
            skCircle(sketch, "E14.2.88.0", {"center": v(4508.5, 201.89) * mm, "radius": 6.35 * mm});
            skCircle(sketch, "E14.0.89.0", {"center": v(4540.25, 201.89) * mm, "radius": 7.94 * mm});
            skCircle(sketch, "E14.2.89.0", {"center": v(4559.3, 201.89) * mm, "radius": 6.35 * mm});
            skCircle(sketch, "E14.0.90.0", {"center": v(4591.05, 201.89) * mm, "radius": 7.94 * mm});
            skCircle(sketch, "E14.2.90.0", {"center": v(4610.1, 201.89) * mm, "radius": 6.35 * mm});
            skCircle(sketch, "E14.0.91.0", {"center": v(4641.85, 201.89) * mm, "radius": 7.94 * mm});
            skCircle(sketch, "E14.2.91.0", {"center": v(4660.9, 201.89) * mm, "radius": 6.35 * mm});
            skCircle(sketch, "E14.0.92.0", {"center": v(4692.65, 201.89) * mm, "radius": 7.94 * mm});
            skCircle(sketch, "E14.2.92.0", {"center": v(4711.7, 201.89) * mm, "radius": 6.35 * mm});
            skCircle(sketch, "E14.0.93.0", {"center": v(4743.45, 201.89) * mm, "radius": 7.94 * mm});
            skCircle(sketch, "E14.2.93.0", {"center": v(4762.5, 201.89) * mm, "radius": 6.35 * mm});
            skCircle(sketch, "E14.0.94.0", {"center": v(4794.25, 201.89) * mm, "radius": 7.94 * mm});
            skCircle(sketch, "E14.2.94.0", {"center": v(4813.3, 201.89) * mm, "radius": 6.35 * mm});
            skCircle(sketch, "E14.0.95.0", {"center": v(4845.05, 201.89) * mm, "radius": 7.94 * mm});
            skCircle(sketch, "E14.2.95.0", {"center": v(4864.1, 201.89) * mm, "radius": 6.35 * mm});
            skCircle(sketch, "E14.0.96.0", {"center": v(4895.85, 201.89) * mm, "radius": 7.94 * mm});
            skCircle(sketch, "E14.2.96.0", {"center": v(4914.9, 201.89) * mm, "radius": 6.35 * mm});
            skCircle(sketch, "E14.0.97.0", {"center": v(4946.65, 201.89) * mm, "radius": 7.94 * mm});
            skCircle(sketch, "E14.2.97.0", {"center": v(4965.7, 201.89) * mm, "radius": 6.35 * mm});
            skCircle(sketch, "E14.0.98.0", {"center": v(4997.45, 201.89) * mm, "radius": 7.94 * mm});
            skCircle(sketch, "E14.2.98.0", {"center": v(5016.5, 201.89) * mm, "radius": 6.35 * mm});
            skCircle(sketch, "E14.0.99.0", {"center": v(5048.25, 201.89) * mm, "radius": 7.94 * mm});
            skCircle(sketch, "E14.2.99.0", {"center": v(5067.3, 201.89) * mm, "radius": 6.35 * mm});
            skSolve(sketch);
        }
        {
            var Q0;
            Q0=makeQuery(id+"F0.imprint","IMPRINT",FACE,{"disambiguationData":[TD([[makeQuery(id+"F0.imprint","IMPRINT",EDGE,{"derivedFrom":sQuery(id+"F0.wireOp",EDGE,"E0.bottom")}),-1.0]])]});
            extrude(context, id + "F1", {"entities" : qUnion([Q0]), "flatOperationType" : FlatOperationType.REMOVE, "depth" : 12.7 * mm, "offsetDistance" : 25.4 * mm, "domain" : OperationDomain.MODEL});
        }
    });
